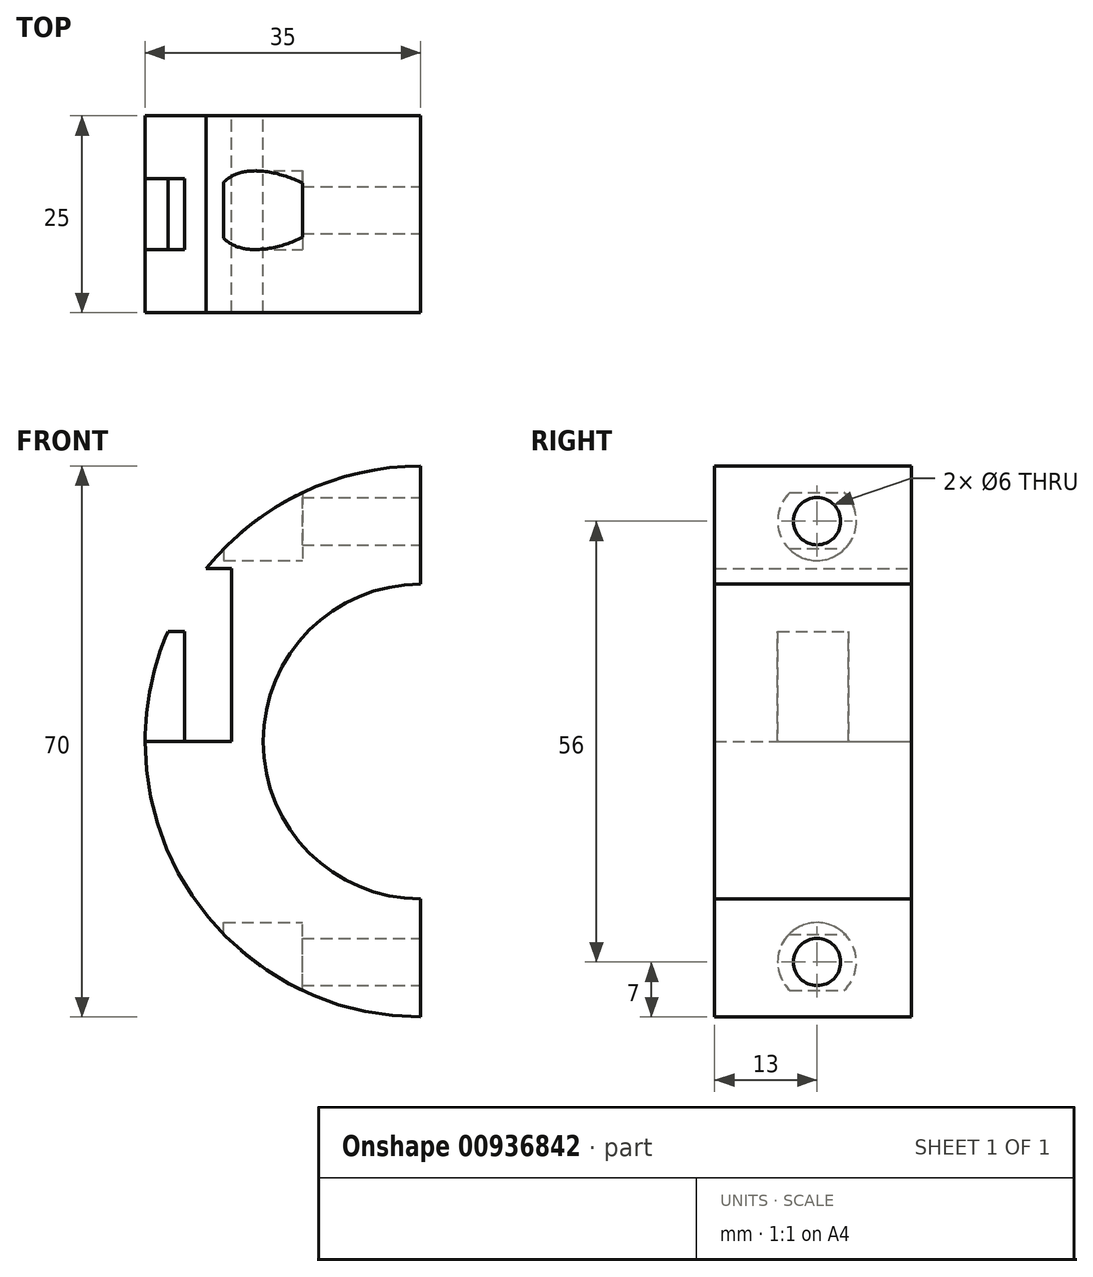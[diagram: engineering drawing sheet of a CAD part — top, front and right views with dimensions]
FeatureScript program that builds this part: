
annotation { "Feature Type Name" : "Feature", "Feature Type Description" : "" }
export const myFeature = defineFeature(function(context is Context, id is Id, definition is map)
    precondition{}
    {
        {
            var Q0;
            Q0=qCreatedBy(makeId("Front.planeOp"),FACE);
            var sketch = newSketch(context, id + "F0", { "sketchPlane" : qUnion([Q0])});
            skArc(sketch, "E0", {"start": v(0, 35) * mm, "mid": v(-35, 0) * mm, "end": v(0, -35) * mm});
            skArc(sketch, "E1", {"start": v(0, 20) * mm, "mid": v(-20, 0) * mm, "end": v(0, -20) * mm});
            skLineSegment(sketch, "E2", {"start": v(0, 20) * mm, "end": v(0, 35) * mm});
            skLineSegment(sketch, "E3", {"start": v(0, -20) * mm, "end": v(0, -35) * mm});
            skSolve(sketch);
        }
        {
            var Q0;
            Q0=makeQuery(id+"F0.imprint","IMPRINT",FACE,{"disambiguationData":[TD([[makeQuery(id+"F0.imprint","IMPRINT",EDGE,{"derivedFrom":sQuery(id+"F0.wireOp",EDGE,"E0")}),1.0]])]});
            extrude(context, id + "F1", {"entities" : qUnion([Q0]), "depth" : 25 * mm, "offsetDistance" : 25 * mm});
        }
        {
            var Q0;
            Q0=qCreatedBy(makeId("Right.planeOp"),FACE);
            var sketch = newSketch(context, id + "F2", { "sketchPlane" : qUnion([Q0])});
            skCircle(sketch, "E4", {"center": v(-12, 28) * mm, "radius": 3 * mm});
            skCircle(sketch, "E5", {"center": v(-12, -28) * mm, "radius": 3 * mm});
            skSolve(sketch);
        }
        {
            var Q0;
            Q0 = qSketchRegion(id + "F2", true);
            var Q1;
            Q1=sQuery(id+"F2.wireOp",EDGE,"E4");
            extrude(context, id + "F3", {"entities" : qUnion([Q0]), "operationType" : NewBodyOperationType.REMOVE, "surfaceEntities" : qUnion([Q1]), "oppositeDirection" : true, "depth" : 25 * mm, "offsetDistance" : 25 * mm});
        }
        {
            var Q0;
            Q0=qCreatedBy(makeId("Right.planeOp"),FACE);
            cPlane(context, id + "F4", {"entities" : qUnion([Q0]), "cplaneType" : CPlaneType.OFFSET, "offset" : 20 * mm, "oppositeDirection" : true, "width" : 150 * mm, "height" : 150 * mm});
        }
        {
            var Q0;
            Q0=qCreatedBy(id+"F4.planeOp",FACE);
            var sketch = newSketch(context, id + "F5", { "sketchPlane" : qUnion([Q0])});
            skCircle(sketch, "E6", {"center": v(-12, 28) * mm, "radius": 5 * mm});
            skCircle(sketch, "E7", {"center": v(-12, -28) * mm, "radius": 5 * mm});
            skSolve(sketch);
        }
        {
            var Q0;
            Q0 = qSketchRegion(id + "F5", true);
            extrude(context, id + "F6", {"entities" : qUnion([Q0]), "operationType" : NewBodyOperationType.REMOVE, "endBound" : BoundingType.SYMMETRIC, "oppositeDirection" : true, "depth" : 10 * mm, "offsetDistance" : 25 * mm});
        }
        {
            var Q0;
            Q0=qCreatedBy(makeId("Front.planeOp"),FACE);
            var sketch = newSketch(context, id + "F7", { "sketchPlane" : qUnion([Q0])});
            skLineSegment(sketch, "E8.bottom", {"start": v(-24, 0) * mm, "end": v(-30, 0) * mm});
            skLineSegment(sketch, "E8.top", {"start": v(-24, 22) * mm, "end": v(-30, 22) * mm});
            skLineSegment(sketch, "E8.left", {"start": v(-24, 0) * mm, "end": v(-24, 22) * mm});
            skLineSegment(sketch, "E8.right", {"start": v(-30, 0) * mm, "end": v(-30, 14) * mm});
            skLineSegment(sketch, "E9.bottom", {"start": v(-24, 22) * mm, "end": v(-44, 22) * mm});
            skLineSegment(sketch, "E9.top", {"start": v(-30, 14) * mm, "end": v(-44, 14) * mm});
            skLineSegment(sketch, "E9.left", {"start": v(-24, 22) * mm, "end": v(-24, 14) * mm});
            skLineSegment(sketch, "E9.right", {"start": v(-44, 22) * mm, "end": v(-44, 14) * mm});
            skSolve(sketch);
        }
        {
            var Q0;
            Q0 = qSketchRegion(id + "F7", true);
            extrude(context, id + "F8", {"entities" : qUnion([Q0]), "operationType" : NewBodyOperationType.REMOVE, "depth" : 28.5 * mm, "offsetDistance" : 25 * mm});
        }
        {
            var Q0;
            Q0=makeQuery(id+"F8.boolean.opBoolean","COPY",FACE,{"derivedFrom":makeQuery(id+"F8.opExtrude","SWEPT_FACE",FACE,{"disambiguationData":[OSD([sQuery(id+"F7.wireOp",EDGE,"E8.left"),sQuery(id+"F7.wireOp",EDGE,"E9.left")])]})});
            var sketch = newSketch(context, id + "F9", { "sketchPlane" : qUnion([Q0])});
            skLineSegment(sketch, "E10.bottom", {"start": v(0, 0) * mm, "end": v(8, 0) * mm});
            skLineSegment(sketch, "E10.top", {"start": v(0, 14) * mm, "end": v(8, 14) * mm});
            skLineSegment(sketch, "E10.left", {"start": v(0, 0) * mm, "end": v(0, 14) * mm});
            skLineSegment(sketch, "E10.right", {"start": v(8, 0) * mm, "end": v(8, 14) * mm});
            skLineSegment(sketch, "E11.bottom", {"start": v(25, 0) * mm, "end": v(17, 0) * mm});
            skLineSegment(sketch, "E11.top", {"start": v(25, 14) * mm, "end": v(17, 14) * mm});
            skLineSegment(sketch, "E11.left", {"start": v(25, 0) * mm, "end": v(25, 14) * mm});
            skLineSegment(sketch, "E11.right", {"start": v(17, 0) * mm, "end": v(17, 14) * mm});
            skSolve(sketch);
        }
        {
            var Q0;
            Q0 = qSketchRegion(id + "F9", true);
            extrude(context, id + "F10", {"entities" : qUnion([Q0]), "operationType" : NewBodyOperationType.REMOVE, "depth" : 25 * mm, "offsetDistance" : 25 * mm});
        }
    });
